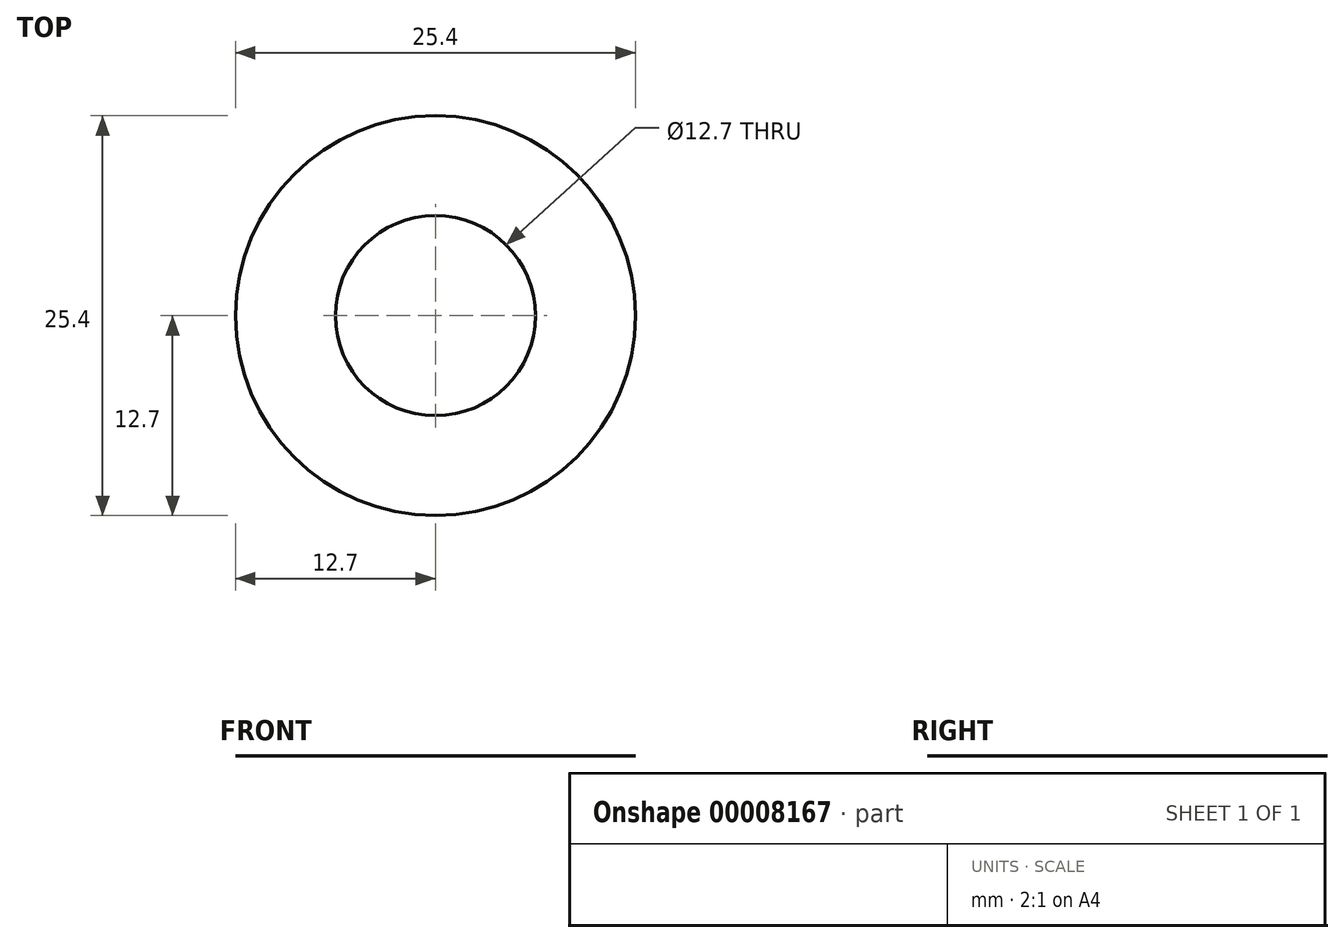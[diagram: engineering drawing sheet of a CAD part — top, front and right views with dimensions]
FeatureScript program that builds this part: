
annotation { "Feature Type Name" : "Feature", "Feature Type Description" : "" }
export const myFeature = defineFeature(function(context is Context, id is Id, definition is map)
    precondition{}
    {
        {
            var Q0;
            Q0=qCreatedBy(makeId("Top.planeOp"),FACE);
            var sketch = newSketch(context, id + "F0", { "sketchPlane" : qUnion([Q0])});
            skCircle(sketch, "E0", {"center": v(0, 0) * mm, "radius": 12.7 * mm});
            skCircle(sketch, "E1", {"center": v(0, 0) * mm, "radius": 6.35 * mm});
            skSolve(sketch);
        }
        {
            var Q0;
            Q0 = qSketchRegion(id + "F0", true);
            extrude(context, id + "F1", {"entities" : qUnion([Q0]), "oppositeDirection" : true, "depth" : 1 / 406.4 * mm});
        }
    });
